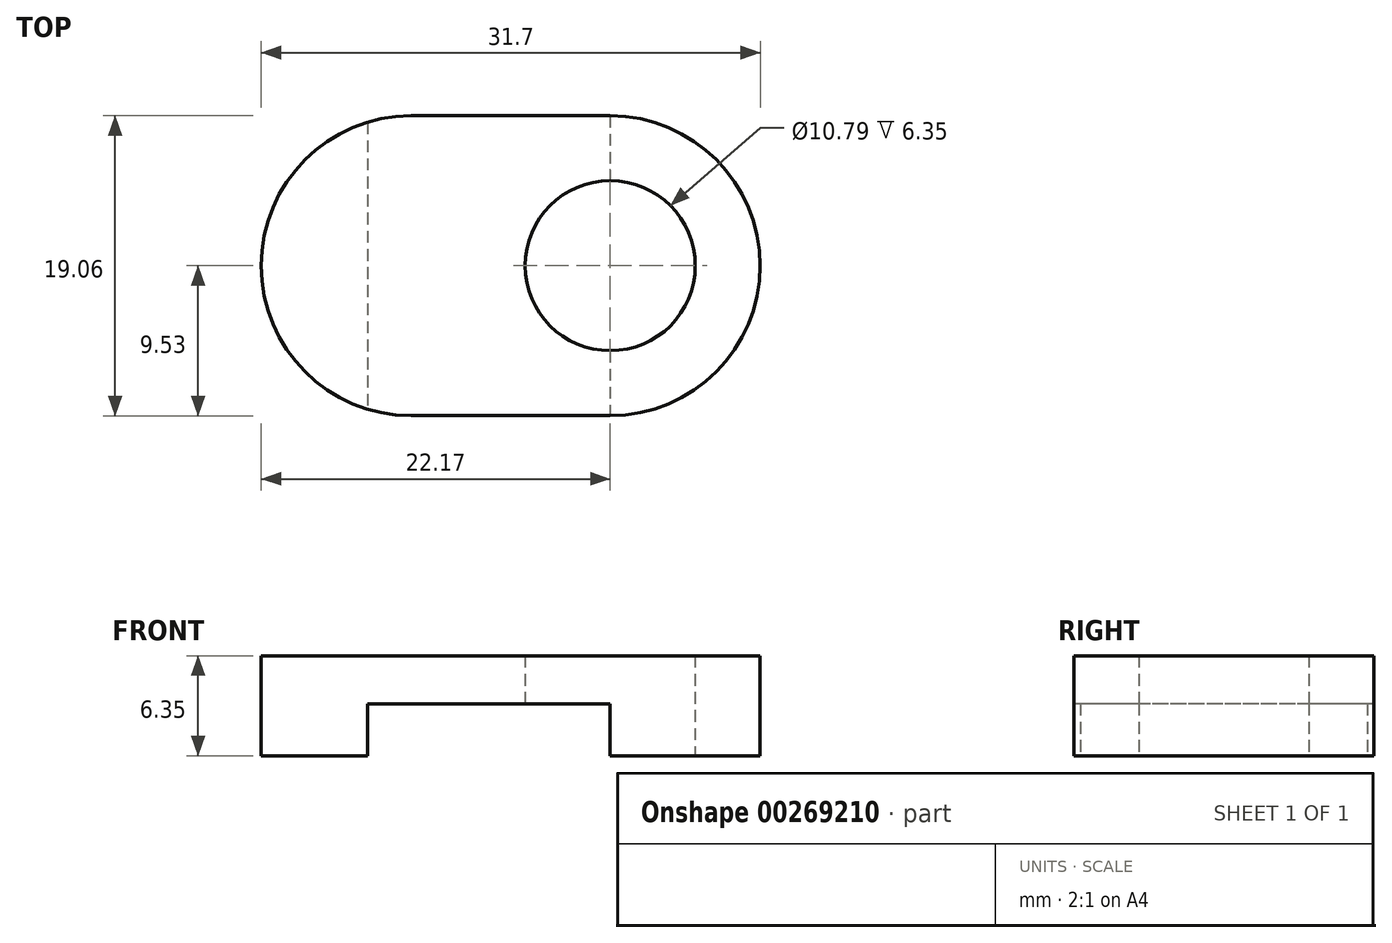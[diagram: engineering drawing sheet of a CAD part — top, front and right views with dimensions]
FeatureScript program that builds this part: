
annotation { "Feature Type Name" : "Feature", "Feature Type Description" : "" }
export const myFeature = defineFeature(function(context is Context, id is Id, definition is map)
    precondition{}
    {
        {
            var Q0;
            Q0=qCreatedBy(makeId("Top.planeOp"),FACE);
            var sketch = newSketch(context, id + "F0", { "sketchPlane" : qUnion([Q0])});
            skCircle(sketch, "E0", {"center": v(0, 0) * mm, "radius": 5.4 * mm});
            skLineSegment(sketch, "E1.bottom", {"start": v(-12.64, 9.53) * mm, "end": v(0, 9.53) * mm});
            skLineSegment(sketch, "E1.top", {"start": v(-12.64, -9.53) * mm, "end": v(0, -9.53) * mm});
            skLineSegment(sketch, "E1.left", {"start": v(-12.64, 9.52) * mm, "end": v(-12.64, -9.53) * mm});
            skLineSegment(sketch, "E2", {"start": v(0, 9.53) * mm, "end": v(0, -9.53) * mm, "construction": true});
            skLineSegment(sketch, "E3", {"start": v(-12.64, 0) * mm, "end": v(12.64, 0) * mm, "construction": true});
            skArc(sketch, "E4", {"start": v(-12.64, 9.52) * mm, "mid": v(-22.17, 0) * mm, "end": v(-12.64, -9.53) * mm});
            skArc(sketch, "E5", {"start": v(0, -9.53) * mm, "mid": v(9.53, 0) * mm, "end": v(0, 9.53) * mm});
            skPoint(sketch, "E6.orphan", {"position": v(12.64, -9.52) * mm});
            skPoint(sketch, "E7.orphan", {"position": v(12.64, 9.53) * mm});
            skSolve(sketch);
        }
        {
            var Q0;
            Q0 = qSketchRegion(id + "F0", true);
            extrude(context, id + "F1", {"entities" : qUnion([Q0]), "depth" : 6.35 * mm});
        }
        {
            var Q0;
            Q0=qCreatedBy(makeId("Front.planeOp"),FACE);
            var sketch = newSketch(context, id + "F2", { "sketchPlane" : qUnion([Q0])});
            skLineSegment(sketch, "E8.bottom", {"start": v(0, 0) * mm, "end": v(-15.42, 0) * mm});
            skLineSegment(sketch, "E8.top", {"start": v(0, 3.3) * mm, "end": v(-15.42, 3.3) * mm});
            skLineSegment(sketch, "E8.left", {"start": v(0, 0) * mm, "end": v(0, 3.3) * mm});
            skLineSegment(sketch, "E8.right", {"start": v(-15.42, 0) * mm, "end": v(-15.42, 3.3) * mm});
            skSolve(sketch);
        }
        {
            var Q0;
            Q0 = qSketchRegion(id + "F2", true);
            extrude(context, id + "F3", {"entities" : qUnion([Q0]), "operationType" : NewBodyOperationType.REMOVE, "oppositeDirection" : true, "depth" : 25.4 * mm, "hasSecondDirection" : true, "secondDirectionOppositeDirection" : false, "secondDirectionDepth" : 25.4 * mm});
        }
    });
